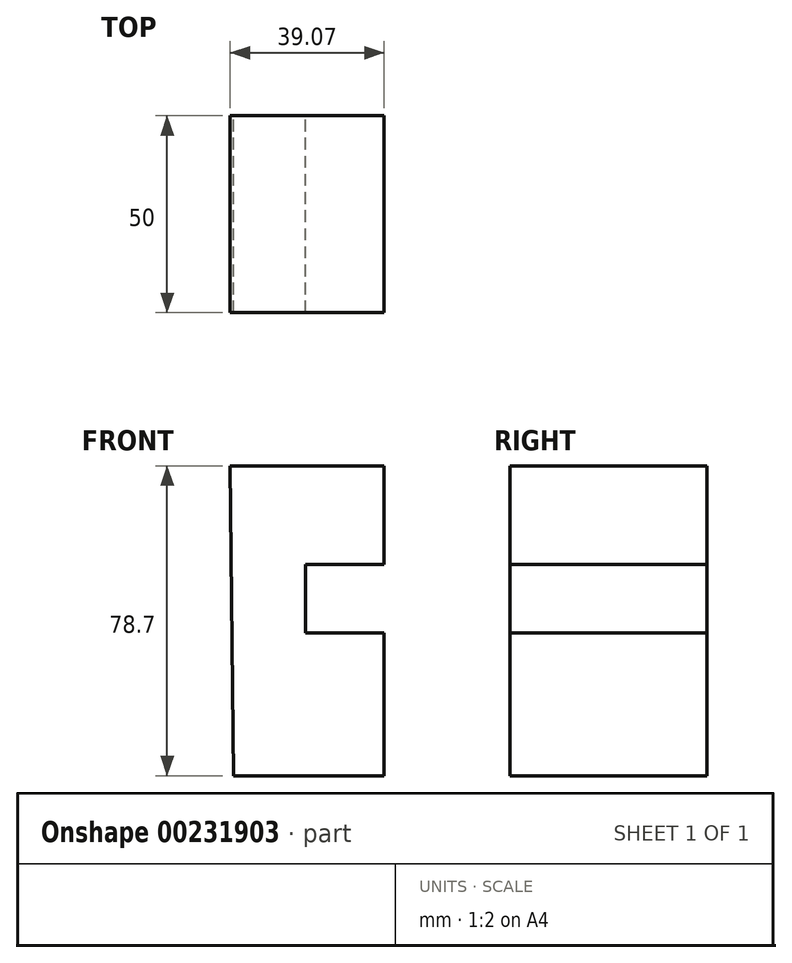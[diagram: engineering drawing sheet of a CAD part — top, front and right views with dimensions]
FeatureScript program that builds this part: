
annotation { "Feature Type Name" : "Feature", "Feature Type Description" : "" }
export const myFeature = defineFeature(function(context is Context, id is Id, definition is map)
    precondition{}
    {
        {
            var Q0;
            Q0=qCreatedBy(makeId("Front.planeOp"),FACE);
            var sketch = newSketch(context, id + "F0", { "sketchPlane" : qUnion([Q0])});
            skLineSegment(sketch, "E0", {"start": v(-39.07, 78.7) * mm, "end": v(0, 78.7) * mm});
            skLineSegment(sketch, "E1", {"start": v(0, 78.7) * mm, "end": v(0, 53.69) * mm});
            skLineSegment(sketch, "E2", {"start": v(0, 53.69) * mm, "end": v(-20, 53.69) * mm});
            skLineSegment(sketch, "E3", {"start": v(-20, 53.69) * mm, "end": v(-20, 36.26) * mm});
            skLineSegment(sketch, "E4", {"start": v(-20, 36.26) * mm, "end": v(0, 36.26) * mm});
            skLineSegment(sketch, "E5", {"start": v(0, 36.26) * mm, "end": v(0, 0) * mm});
            skLineSegment(sketch, "E6", {"start": v(0, 0) * mm, "end": v(-38.23, 0) * mm});
            skLineSegment(sketch, "E7", {"start": v(-38.23, 0) * mm, "end": v(-39.07, 78.7) * mm});
            skSolve(sketch);
        }
        {
            var Q0;
            Q0 = qSketchRegion(id + "F0", true);
            extrude(context, id + "F1", {"entities" : qUnion([Q0]), "depth" : 25 * mm, "hasSecondDirection" : true, "secondDirectionOppositeDirection" : true, "secondDirectionDepth" : 25 * mm});
        }
    });
